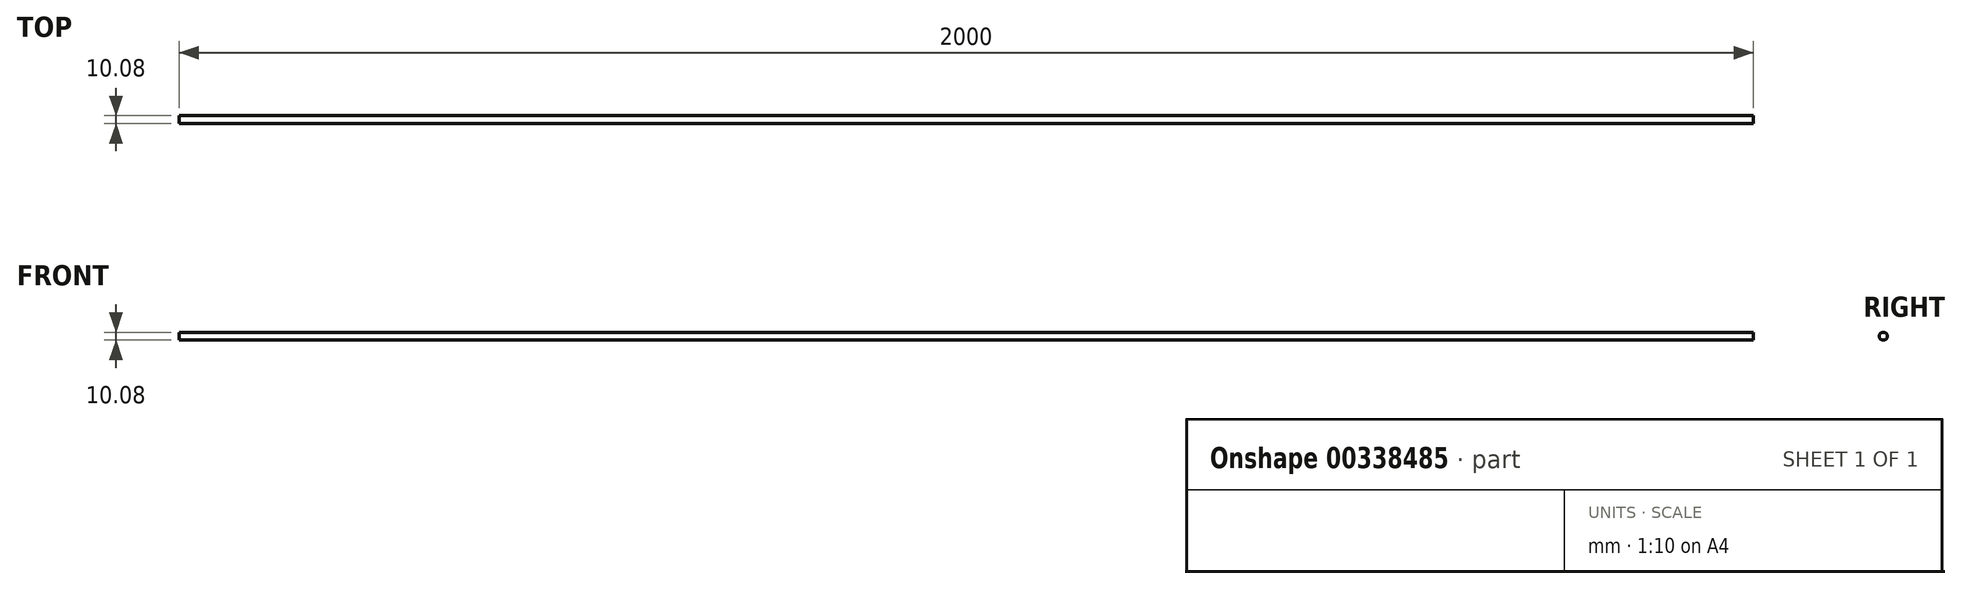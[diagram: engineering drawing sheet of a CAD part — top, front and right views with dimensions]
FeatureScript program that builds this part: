
annotation { "Feature Type Name" : "Feature", "Feature Type Description" : "" }
export const myFeature = defineFeature(function(context is Context, id is Id, definition is map)
    precondition{}
    {
        {
            var Q0;
            Q0=qCreatedBy(makeId("Right.planeOp"),FACE);
            var sketch = newSketch(context, id + "F0", { "sketchPlane" : qUnion([Q0])});
            skCircle(sketch, "E0", {"center": v(0, 0) * mm, "radius": 5.04 * mm});
            skSolve(sketch);
        }
        {
            var Q0;
            Q0=makeQuery(id+"F0.imprint","IMPRINT",FACE,{"disambiguationData":[TD([[makeQuery(id+"F0.imprint","IMPRINT",EDGE,{"derivedFrom":sQuery(id+"F0.wireOp",EDGE,"E0")}),1.0]])]});
            extrude(context, id + "F1", {"entities" : qUnion([Q0]), "depth" : 2000 * mm});
        }
    });
